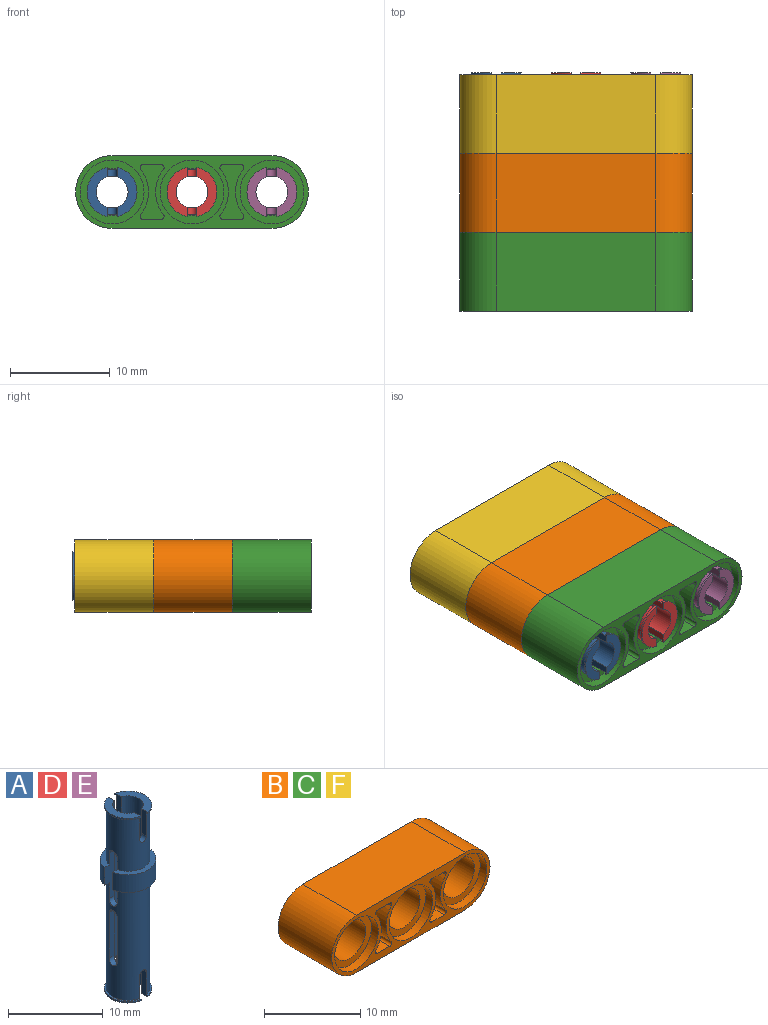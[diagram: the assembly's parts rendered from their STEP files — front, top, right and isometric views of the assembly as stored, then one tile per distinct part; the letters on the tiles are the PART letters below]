
ASSEMBLY  parts=6 mates=7
PART A: 49 faces, bbox 5.8x5.9x23.9 mm
  f0: cylinder r=2.95mm len=5.78mm, axis (0,0,-1), area 18.5mm2, adj f1,f2,f33,f40
  f1: plane 5.78x2.35mm, normal (0,0,1), area 4.6mm2, adj f0,f9,f33,f40
  f2: plane 5.78x2.35mm, normal (0,0,-1), area 4.6mm2, adj f0,f10,f33,f40
  f3: plane 4.9x2mm, normal (0,0,-1), area 4.9mm2, adj f11,f18,f21,f32
  f4: plane 4.9x2mm, normal (0,0,1), area 1.3mm2, adj f5,f10,f19,f20
  f5: cylinder r=2.5mm len=4.9mm, axis (0,0,1), area 1.4mm2, adj f4,f16,f19,f20
  f6: plane 4.9x2mm, normal (0,0,1), area 4.9mm2, adj f11,f23,f28,f30
  f7: plane 4.9x2mm, normal (0,0,-1), area 1.3mm2, adj f8,f9,f24,f27
  f8: cylinder r=2.5mm len=4.9mm, axis (0,0,-1), area 1.4mm2, adj f7,f14,f24,f27
  f9: cylinder r=2.3mm len=6.8mm, axis (0,0,1), area 86.6mm2, adj f1,f7,f13,f23,f24,f25,f26,f27
  f10: cylinder r=2.3mm len=14.4mm, axis (0,0,-1), area 178.6mm2, adj f2,f4,f15,f17,f18,f19,f20,f21
  f11: cylinder r=1.6mm len=23.9mm, axis (0,0,1), area 192.2mm2, adj f3,f6,f14,f16,f17,f18,f19,f20
  f12: cylinder r=2.95mm len=5.78mm, axis (0,0,-1), area 18.5mm2, adj f13,f15,f34,f39
  f13: plane 5.78x2.35mm, normal (0,0,1), area 4.6mm2, adj f9,f12,f34,f39
  f14: plane 4.9x2mm, normal (0,0,1), area 4.9mm2, adj f8,f11,f24,f27
  f15: plane 5.78x2.35mm, normal (0,0,-1), area 4.6mm2, adj f10,f12,f34,f39
  f16: plane 4.9x2mm, normal (0,0,-1), area 4.9mm2, adj f5,f11,f19,f20
  f17: cylinder r=0.5mm len=1mm, axis (0,-1,0), area 1.1mm2, adj f10,f11,f18,f19
  f18: plane 3.15x0.93mm, normal (-1,0,0), area 2.3mm2, adj f3,f10,f11,f17,f31,f32
  f19: plane 3.15x0.93mm, normal (1,0,0), area 2.3mm2, adj f4,f5,f10,f11,f16,f17
  f20: plane 3.15x0.93mm, normal (1,0,0), area 2.3mm2, adj f4,f5,f10,f11,f16,f22
  f21: plane 3.15x0.93mm, normal (-1,0,0), area 2.3mm2, adj f3,f10,f11,f22,f31,f32
  f22: cylinder r=0.5mm len=1mm, axis (0,-1,0), area 1.1mm2, adj f10,f11,f20,f21
  f23: plane 3.15x0.93mm, normal (1,0,0), area 2.3mm2, adj f6,f9,f11,f25,f29,f30
  f24: plane 3.15x0.93mm, normal (-1,0,0), area 2.3mm2, adj f7,f8,f9,f11,f14,f25
  f25: cylinder r=0.5mm len=1mm, axis (0,-1,0), area 1.1mm2, adj f9,f11,f23,f24
  f26: cylinder r=0.5mm len=1mm, axis (0,-1,0), area 1.1mm2, adj f9,f11,f27,f28
  f27: plane 3.15x0.93mm, normal (-1,0,0), area 2.3mm2, adj f7,f8,f9,f11,f14,f26
  f28: plane 3.15x0.93mm, normal (1,0,0), area 2.3mm2, adj f6,f9,f11,f26,f29,f30
  f29: plane 4.9x2mm, normal (0,0,-1), area 1.3mm2, adj f9,f23,f28,f30
  f30: cylinder r=2.5mm len=4.9mm, axis (0,0,-1), area 1.4mm2, adj f6,f23,f28,f29
  f31: plane 4.9x2mm, normal (0,0,1), area 1.3mm2, adj f10,f18,f21,f32
  f32: cylinder r=2.5mm len=4.9mm, axis (0,0,1), area 1.4mm2, adj f3,f18,f21,f31
  f33: plane 5.9x1.41mm, normal (0,1,0), area 5.9mm2, adj f0,f1,f2,f9,f10,f11,f35,f36
  f34: plane 5.9x1.41mm, normal (0,-1,0), area 5.9mm2, adj f9,f10,f11,f12,f13,f15,f35,f36
  f35: cylinder r=0.6mm len=1.2mm, axis (1,0,0), area 1.4mm2, adj f9,f11,f33,f34
  f36: cylinder r=0.6mm len=1.2mm, axis (1,0,0), area 1.4mm2, adj f10,f11,f33,f34
  f37: cylinder r=0.6mm len=1.2mm, axis (1,0,0), area 1.4mm2, adj f10,f11,f39,f40
  f38: cylinder r=0.6mm len=1.2mm, axis (1,0,0), area 1.4mm2, adj f9,f11,f39,f40
  f39: plane 5.9x1.41mm, normal (0,-1,0), area 5.9mm2, adj f9,f10,f11,f12,f13,f15,f37,f38
  f40: plane 5.9x1.41mm, normal (0,1,0), area 5.9mm2, adj f0,f1,f2,f9,f10,f11,f37,f38
  f41: plane 5.9x0.74mm, normal (0,1,0), area 4.3mm2, adj f10,f11,f42,f44
  f42: cylinder r=0.6mm len=1.2mm, axis (1,0,0), area 1.4mm2, adj f10,f11,f41,f43
  f43: plane 5.9x0.74mm, normal (0,-1,0), area 4.3mm2, adj f10,f11,f42,f44
  f44: cylinder r=0.6mm len=1.2mm, axis (1,0,0), area 1.4mm2, adj f10,f11,f41,f43
  f45: cylinder r=0.6mm len=1.2mm, axis (1,0,0), area 1.4mm2, adj f10,f11,f46,f48
  f46: plane 5.9x0.74mm, normal (0,-1,0), area 4.3mm2, adj f10,f11,f45,f47
  f47: cylinder r=0.6mm len=1.2mm, axis (1,0,0), area 1.4mm2, adj f10,f11,f46,f48
  f48: plane 5.9x0.74mm, normal (0,1,0), area 4.3mm2, adj f10,f11,f45,f47
PART B: 57 faces, bbox 23.3x7.9x7.3 mm
  f0: plane 23.3x7.3mm, normal (0,1,0), area 46.8mm2, adj f5,f6,f7,f8,f15,f17,f19,f31
  f1: plane 23.3x7.3mm, normal (0,-1,0), area 46.8mm2, adj f5,f6,f7,f8,f9,f11,f13,f21
  f2: cylinder r=2.35mm len=5.9mm, axis (0,-1,0), area 87.1mm2, adj f10,f20
  f3: cylinder r=2.35mm len=5.9mm, axis (0,-1,0), area 87.1mm2, adj f12,f18
  f4: cylinder r=2.35mm len=5.9mm, axis (0,-1,0), area 87.1mm2, adj f14,f16
  f5: plane 16x7.9mm, normal (0,0,1), area 126.4mm2, adj f0,f1,f6,f8
  f6: cylinder r=3.65mm len=7.9mm, axis (0,1,0), area 90.6mm2, adj f0,f1,f5,f7
  f7: plane 16x7.9mm, normal (0,0,-1), area 126.4mm2, adj f0,f1,f6,f8
  f8: cylinder r=3.65mm len=7.9mm, axis (0,1,0), area 90.6mm2, adj f0,f1,f5,f7
  f9: cylinder r=3.2mm len=6.4mm, axis (0,-1,0), area 20.1mm2, adj f1,f10
  f10: plane 6.4x6.4mm, normal (0,-1,0), area 14.8mm2, adj f2,f9
  f11: cylinder r=3.2mm len=6.4mm, axis (0,-1,0), area 20.1mm2, adj f1,f12
  f12: plane 6.4x6.4mm, normal (0,-1,0), area 14.8mm2, adj f3,f11
  f13: cylinder r=3.2mm len=6.4mm, axis (0,-1,0), area 20.1mm2, adj f1,f14
  f14: plane 6.4x6.4mm, normal (0,-1,0), area 14.8mm2, adj f4,f13
  f15: cylinder r=3.2mm len=6.4mm, axis (0,1,0), area 20.1mm2, adj f0,f16
  f16: plane 6.4x6.4mm, normal (0,1,0), area 14.8mm2, adj f4,f15
  f17: cylinder r=3.2mm len=6.4mm, axis (0,1,0), area 20.1mm2, adj f0,f18
  f18: plane 6.4x6.4mm, normal (0,1,0), area 14.8mm2, adj f3,f17
  f19: cylinder r=3.2mm len=6.4mm, axis (0,1,0), area 20.1mm2, adj f0,f20
  f20: plane 6.4x6.4mm, normal (0,1,0), area 14.8mm2, adj f2,f19
  f21: cylinder r=3.65mm len=4.53mm, axis (0,-1,0), area 17.6mm2, adj f1,f25,f49,f52
  f22: plane 3.6x1.8mm, normal (0,0,-1), area 6.5mm2, adj f1,f25,f49,f50
  f23: cylinder r=3.65mm len=4.53mm, axis (0,-1,0), area 17.6mm2, adj f1,f25,f50,f51
  f24: plane 3.6x1.8mm, normal (0,0,1), area 6.5mm2, adj f1,f25,f51,f52
  f25: plane 5.5x2.4mm, normal (0,-1,0), area 7.7mm2, adj f21,f22,f23,f24,f49,f50,f51,f52
  f26: plane 3.6x1.8mm, normal (0,0,-1), area 6.5mm2, adj f1,f30,f53,f56
  f27: cylinder r=3.65mm len=4.53mm, axis (0,-1,0), area 17.6mm2, adj f1,f30,f55,f56
  f28: plane 3.6x1.8mm, normal (0,0,1), area 6.5mm2, adj f1,f30,f54,f55
  f29: cylinder r=3.65mm len=4.53mm, axis (0,-1,0), area 17.6mm2, adj f1,f30,f53,f54
  f30: plane 5.5x2.4mm, normal (0,-1,0), area 7.7mm2, adj f26,f27,f28,f29,f53,f54,f55,f56
  f31: cylinder r=3.65mm len=4.53mm, axis (0,1,0), area 17.6mm2, adj f0,f35,f41,f44
  f32: plane 3.6x1.8mm, normal (0,0,-1), area 6.5mm2, adj f0,f35,f41,f42
  f33: cylinder r=3.65mm len=4.53mm, axis (0,1,0), area 17.6mm2, adj f0,f35,f42,f43
  f34: plane 3.6x1.8mm, normal (0,0,1), area 6.5mm2, adj f0,f35,f43,f44
  f35: plane 5.5x2.4mm, normal (0,1,0), area 7.7mm2, adj f31,f32,f33,f34,f41,f42,f43,f44
  f36: cylinder r=3.65mm len=4.53mm, axis (0,1,0), area 17.6mm2, adj f0,f40,f45,f48
  f37: plane 3.6x1.8mm, normal (0,0,-1), area 6.5mm2, adj f0,f40,f47,f48
  f38: cylinder r=3.65mm len=4.53mm, axis (0,1,0), area 17.6mm2, adj f0,f40,f46,f47
  f39: plane 3.6x1.8mm, normal (0,0,1), area 6.5mm2, adj f0,f40,f45,f46
  f40: plane 5.5x2.4mm, normal (0,1,0), area 7.7mm2, adj f36,f37,f38,f39,f45,f46,f47,f48
  f41: cylinder r=0.3mm len=3.6mm, axis (0,1,0), area 2.4mm2, adj f0,f31,f32,f35
  f42: cylinder r=0.3mm len=3.6mm, axis (0,1,0), area 2.4mm2, adj f0,f32,f33,f35
  f43: cylinder r=0.3mm len=3.6mm, axis (0,1,0), area 2.4mm2, adj f0,f33,f34,f35
  f44: cylinder r=0.3mm len=3.6mm, axis (0,1,0), area 2.4mm2, adj f0,f31,f34,f35
  f45: cylinder r=0.3mm len=3.6mm, axis (0,1,0), area 2.4mm2, adj f0,f36,f39,f40
  f46: cylinder r=0.3mm len=3.6mm, axis (0,1,0), area 2.4mm2, adj f0,f38,f39,f40
  f47: cylinder r=0.3mm len=3.6mm, axis (0,1,0), area 2.4mm2, adj f0,f37,f38,f40
  f48: cylinder r=0.3mm len=3.6mm, axis (0,1,0), area 2.4mm2, adj f0,f36,f37,f40
  f49: cylinder r=0.3mm len=3.6mm, axis (0,-1,0), area 2.4mm2, adj f1,f21,f22,f25
  f50: cylinder r=0.3mm len=3.6mm, axis (0,-1,0), area 2.4mm2, adj f1,f22,f23,f25
  f51: cylinder r=0.3mm len=3.6mm, axis (0,-1,0), area 2.4mm2, adj f1,f23,f24,f25
  f52: cylinder r=0.3mm len=3.6mm, axis (0,-1,0), area 2.4mm2, adj f1,f21,f24,f25
  f53: cylinder r=0.3mm len=3.6mm, axis (0,-1,0), area 2.4mm2, adj f1,f26,f29,f30
  f54: cylinder r=0.3mm len=3.6mm, axis (0,-1,0), area 2.4mm2, adj f1,f28,f29,f30
  f55: cylinder r=0.3mm len=3.6mm, axis (0,-1,0), area 2.4mm2, adj f1,f27,f28,f30
  f56: cylinder r=0.3mm len=3.6mm, axis (0,-1,0), area 2.4mm2, adj f1,f26,f27,f30
PART C: same geometry as B
PART D: same geometry as A
PART E: same geometry as A
PART F: same geometry as B
PLACE A rot(axis=(1,0,0),90deg) t=(-7.48,-10.78,0.54)mm
PLACE B t=(0.52,-6.93,0.54)mm
PLACE C t=(0.52,-14.83,0.54)mm
PLACE D rot(axis=(1,0,0),90deg) t=(0.52,-10.78,0.54)mm
PLACE E rot(axis=(1,0,0),90deg) t=(8.52,-10.78,0.54)mm
PLACE F t=(0.52,0.97,0.54)mm
MATE fastened B.f3 <-> C.f3  axis (0,-1,0) through (0.52,-14.83,0.54)mm
MATE fastened E.f5 <-> C.f2  axis (0,-1,0) through (8.52,-22.73,0.54)mm
MATE fastened D.f5 <-> C.f3  axis (0,-1,0) through (0.52,-22.73,0.54)mm
MATE fastened B.f3 <-> B.f2  axis (0,-1,0) through (0.52,-14.83,0.54)mm
MATE fastened A.f5 <-> C.f4  axis (0,-1,0) through (-7.48,-22.73,0.54)mm
MATE fastened F.f4 <-> B.f4  axis (0,-1,0) through (-7.48,-6.93,0.54)mm
MATE fastened B.f4 <-> B.f2  axis (0,-1,0) through (-7.48,-14.83,0.54)mm
